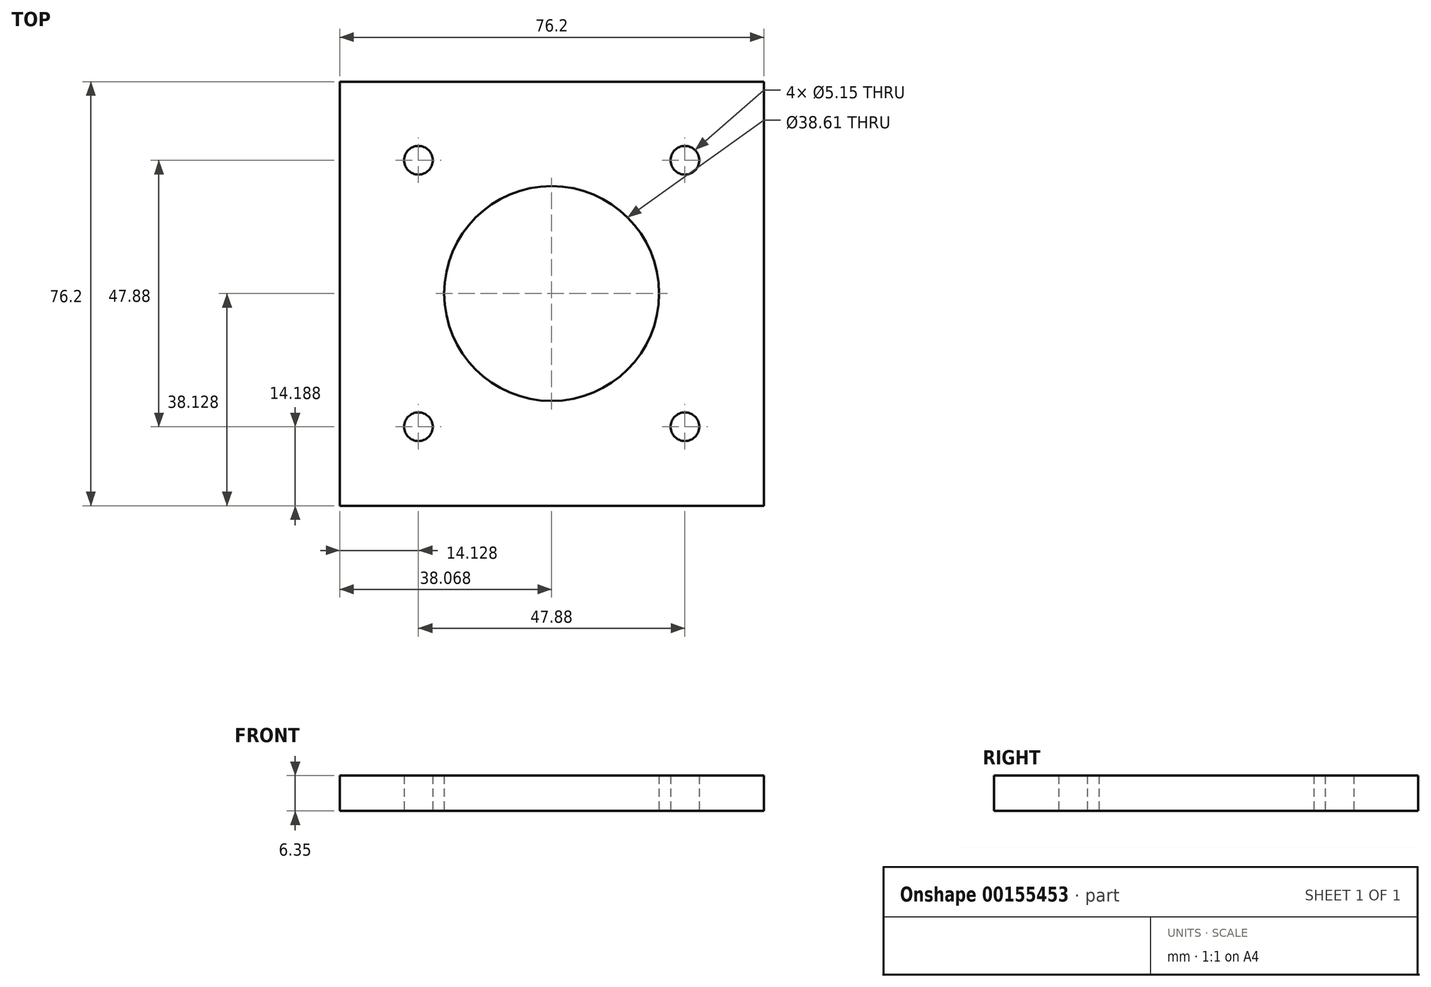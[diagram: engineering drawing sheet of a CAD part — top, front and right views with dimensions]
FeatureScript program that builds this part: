
annotation { "Feature Type Name" : "Feature", "Feature Type Description" : "" }
export const myFeature = defineFeature(function(context is Context, id is Id, definition is map)
    precondition{}
    {
        {
            var Q0;
            Q0=qCreatedBy(makeId("Top.planeOp"),FACE);
            var sketch = newSketch(context, id + "F0", { "sketchPlane" : qUnion([Q0])});
            skCircle(sketch, "E0.0", {"center": v(-23.97, -23.91) * mm, "radius": 2.57 * mm});
            skCircle(sketch, "E1.0", {"center": v(-23.97, 23.97) * mm, "radius": 2.57 * mm});
            skCircle(sketch, "E2.0", {"center": v(23.9, 23.97) * mm, "radius": 2.57 * mm});
            skCircle(sketch, "E3.0", {"center": v(23.9, -23.91) * mm, "radius": 2.57 * mm});
            skCircle(sketch, "E4.0", {"center": v(-0.03, 0.03) * mm, "radius": 19.3 * mm});
            skLineSegment(sketch, "E5.bottom", {"start": v(-38.1, 38.1) * mm, "end": v(38.1, 38.1) * mm});
            skLineSegment(sketch, "E5.top", {"start": v(-38.1, -38.1) * mm, "end": v(38.1, -38.1) * mm});
            skLineSegment(sketch, "E5.left", {"start": v(-38.1, 38.1) * mm, "end": v(-38.1, -38.1) * mm});
            skLineSegment(sketch, "E5.right", {"start": v(38.1, 38.1) * mm, "end": v(38.1, -38.1) * mm});
            skSolve(sketch);
        }
        {
            var Q0;
            Q0 = qSketchRegion(id + "F0", true);
            extrude(context, id + "F1", {"entities" : qUnion([Q0]), "depth" : 6.35 * mm});
        }
    });
